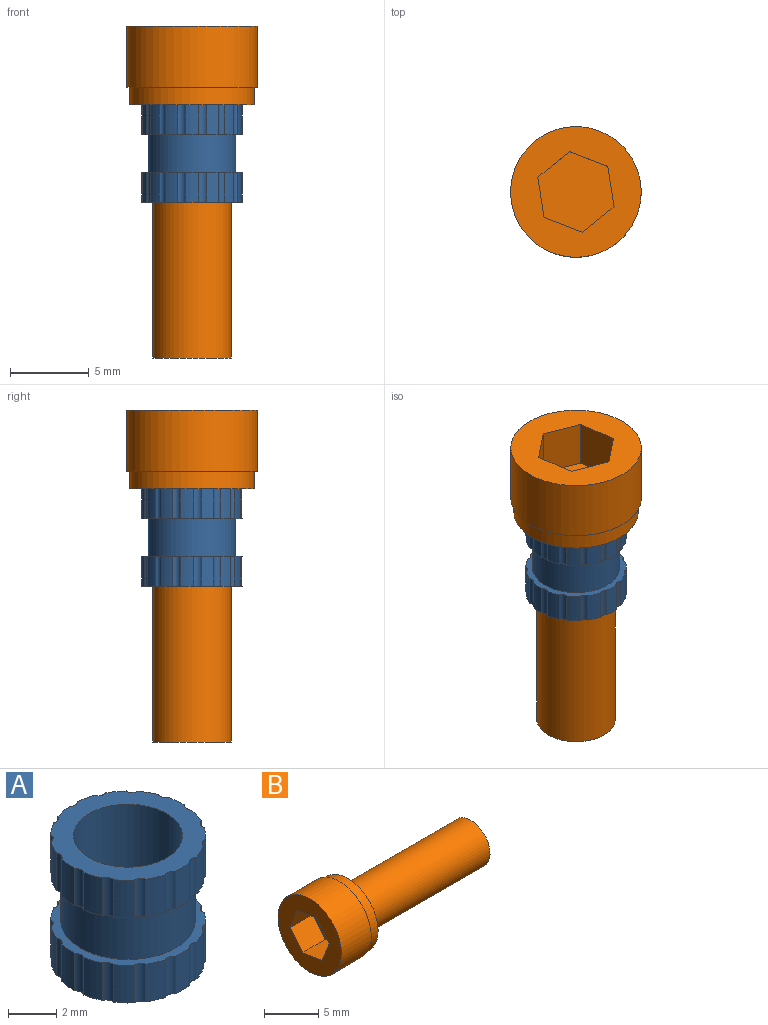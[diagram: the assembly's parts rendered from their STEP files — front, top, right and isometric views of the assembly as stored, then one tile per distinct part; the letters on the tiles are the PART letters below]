
ASSEMBLY  parts=2 mates=1
PART A: 66 faces, bbox 6.4x6.4x6.2 mm
  f0: cylinder r=3.2mm len=1.9mm, axis (0,0,-1), area 1.6mm2, adj f2,f57,f59,f65
  f1: cylinder r=3.2mm len=1.9mm, axis (0,0,-1), area 1.6mm2, adj f3,f61,f63,f64
  f2: cylinder r=0.38mm len=1.9mm, axis (0,0,1), area 1mm2, adj f0,f4,f57,f59
  f3: cylinder r=0.38mm len=1.9mm, axis (0,0,1), area 1mm2, adj f1,f5,f61,f63
  f4: cylinder r=3.2mm len=1.9mm, axis (0,0,-1), area 1.6mm2, adj f2,f6,f57,f59
  f5: cylinder r=3.2mm len=1.9mm, axis (0,0,-1), area 1.6mm2, adj f3,f7,f61,f63
  f6: cylinder r=0.38mm len=1.9mm, axis (0,0,1), area 1mm2, adj f4,f8,f57,f59
  f7: cylinder r=0.38mm len=1.9mm, axis (0,0,1), area 1mm2, adj f5,f9,f61,f63
  f8: cylinder r=3.2mm len=1.9mm, axis (0,0,-1), area 1.6mm2, adj f6,f10,f57,f59
  f9: cylinder r=3.2mm len=1.9mm, axis (0,0,-1), area 1.6mm2, adj f7,f11,f61,f63
  f10: cylinder r=0.38mm len=1.9mm, axis (0,0,1), area 1mm2, adj f8,f12,f57,f59
  f11: cylinder r=0.38mm len=1.9mm, axis (0,0,1), area 1mm2, adj f9,f13,f61,f63
  f12: cylinder r=3.2mm len=1.9mm, axis (0,0,-1), area 1.6mm2, adj f10,f14,f57,f59
  f13: cylinder r=3.2mm len=1.9mm, axis (0,0,-1), area 1.6mm2, adj f11,f15,f61,f63
  f14: cylinder r=0.38mm len=1.9mm, axis (0,0,1), area 1mm2, adj f12,f16,f57,f59
  f15: cylinder r=0.38mm len=1.9mm, axis (0,0,1), area 1mm2, adj f13,f17,f61,f63
  f16: cylinder r=3.2mm len=1.9mm, axis (0,0,-1), area 1.6mm2, adj f14,f18,f57,f59
  f17: cylinder r=3.2mm len=1.9mm, axis (0,0,-1), area 1.6mm2, adj f15,f19,f61,f63
  f18: cylinder r=0.38mm len=1.9mm, axis (0,0,1), area 1mm2, adj f16,f20,f57,f59
  f19: cylinder r=0.38mm len=1.9mm, axis (0,0,1), area 1mm2, adj f17,f21,f61,f63
  f20: cylinder r=3.2mm len=1.9mm, axis (0,0,-1), area 1.6mm2, adj f18,f22,f57,f59
  f21: cylinder r=3.2mm len=1.9mm, axis (0,0,-1), area 1.6mm2, adj f19,f23,f61,f63
  f22: cylinder r=0.38mm len=1.9mm, axis (0,0,1), area 1mm2, adj f20,f24,f57,f59
  f23: cylinder r=0.38mm len=1.9mm, axis (0,0,1), area 1mm2, adj f21,f25,f61,f63
  f24: cylinder r=3.2mm len=1.9mm, axis (0,0,-1), area 1.6mm2, adj f22,f26,f57,f59
  f25: cylinder r=3.2mm len=1.9mm, axis (0,0,-1), area 1.6mm2, adj f23,f27,f61,f63
  f26: cylinder r=0.38mm len=1.9mm, axis (0,0,1), area 1mm2, adj f24,f28,f57,f59
  f27: cylinder r=0.38mm len=1.9mm, axis (0,0,1), area 1mm2, adj f25,f29,f61,f63
  f28: cylinder r=3.2mm len=1.9mm, axis (0,0,-1), area 1.6mm2, adj f26,f30,f57,f59
  f29: cylinder r=3.2mm len=1.9mm, axis (0,0,-1), area 1.6mm2, adj f27,f31,f61,f63
  f30: cylinder r=0.38mm len=1.9mm, axis (0,0,1), area 1mm2, adj f28,f32,f57,f59
  f31: cylinder r=0.38mm len=1.9mm, axis (0,0,1), area 1mm2, adj f29,f33,f61,f63
  f32: cylinder r=3.2mm len=1.9mm, axis (0,0,-1), area 1.6mm2, adj f30,f34,f57,f59
  f33: cylinder r=3.2mm len=1.9mm, axis (0,0,-1), area 1.6mm2, adj f31,f35,f61,f63
  f34: cylinder r=0.38mm len=1.9mm, axis (0,0,1), area 1mm2, adj f32,f36,f57,f59
  f35: cylinder r=0.38mm len=1.9mm, axis (0,0,1), area 1mm2, adj f33,f37,f61,f63
  f36: cylinder r=3.2mm len=1.9mm, axis (0,0,-1), area 1.6mm2, adj f34,f38,f57,f59
  f37: cylinder r=3.2mm len=1.9mm, axis (0,0,-1), area 1.6mm2, adj f35,f39,f61,f63
  f38: cylinder r=0.38mm len=1.9mm, axis (0,0,1), area 1mm2, adj f36,f40,f57,f59
  f39: cylinder r=0.38mm len=1.9mm, axis (0,0,1), area 1mm2, adj f37,f41,f61,f63
  f40: cylinder r=3.2mm len=1.9mm, axis (0,0,-1), area 1.6mm2, adj f38,f42,f57,f59
  f41: cylinder r=3.2mm len=1.9mm, axis (0,0,-1), area 1.6mm2, adj f39,f43,f61,f63
  f42: cylinder r=0.38mm len=1.9mm, axis (0,0,1), area 1mm2, adj f40,f44,f57,f59
  f43: cylinder r=0.38mm len=1.9mm, axis (0,0,1), area 1mm2, adj f41,f45,f61,f63
  f44: cylinder r=3.2mm len=1.9mm, axis (0,0,-1), area 1.6mm2, adj f42,f46,f57,f59
  f45: cylinder r=3.2mm len=1.9mm, axis (0,0,-1), area 1.6mm2, adj f43,f47,f61,f63
  f46: cylinder r=0.38mm len=1.9mm, axis (0,0,1), area 1mm2, adj f44,f48,f57,f59
  f47: cylinder r=0.38mm len=1.9mm, axis (0,0,1), area 1mm2, adj f45,f49,f61,f63
  f48: cylinder r=3.2mm len=1.9mm, axis (0,0,-1), area 1.6mm2, adj f46,f50,f57,f59
  f49: cylinder r=3.2mm len=1.9mm, axis (0,0,-1), area 1.6mm2, adj f47,f51,f61,f63
  f50: cylinder r=0.38mm len=1.9mm, axis (0,0,1), area 1mm2, adj f48,f52,f57,f59
  f51: cylinder r=0.38mm len=1.9mm, axis (0,0,1), area 1mm2, adj f49,f53,f61,f63
  f52: cylinder r=3.2mm len=1.9mm, axis (0,0,-1), area 1.6mm2, adj f50,f54,f57,f59
  f53: cylinder r=3.2mm len=1.9mm, axis (0,0,-1), area 1.6mm2, adj f51,f55,f61,f63
  f54: cylinder r=0.38mm len=1.9mm, axis (0,0,1), area 1mm2, adj f52,f57,f58,f59
  f55: cylinder r=0.38mm len=1.9mm, axis (0,0,1), area 1mm2, adj f53,f61,f62,f63
  f56: cylinder r=2.25mm len=6.2mm, axis (0,0,-1), area 87.7mm2, adj f57,f63
  f57: plane 6.4x6.39mm, normal (0,0,-1), area 15.8mm2, adj f0,f2,f4,f6,f8,f10,f12,f14
  f58: cylinder r=3.2mm len=1.9mm, axis (0,0,-1), area 1.6mm2, adj f54,f57,f59,f65
  f59: plane 6.4x6.39mm, normal (0,0,1), area 7.5mm2, adj f0,f2,f4,f6,f8,f10,f12,f14
  f60: cylinder r=2.77mm len=5.55mm, axis (0,0,-1), area 41.8mm2, adj f59,f61
  f61: plane 6.4x6.39mm, normal (0,0,-1), area 7.5mm2, adj f1,f3,f5,f7,f9,f11,f13,f15
  f62: cylinder r=3.2mm len=1.9mm, axis (0,0,-1), area 1.6mm2, adj f55,f61,f63,f64
  f63: plane 6.4x6.39mm, normal (0,0,1), area 15.8mm2, adj f1,f3,f5,f7,f9,f11,f13,f15
  f64: cylinder r=0.38mm len=1.9mm, axis (0,0,1), area 1mm2, adj f1,f61,f62,f63
  f65: cylinder r=0.38mm len=1.9mm, axis (0,0,1), area 1mm2, adj f0,f57,f58,f59
PART B: 14 faces, bbox 21.1x8.3x8.3 mm
  f0: cylinder r=2.5mm len=16.1mm, axis (-1,0,0), area 252.9mm2, adj f1,f3
  f1: plane 5x5mm, normal (1,0,0), area 19.6mm2, adj f0
  f2: plane 8.3x8.3mm, normal (-1,0,0), area 36.6mm2, adj f6,f7,f8,f9,f10,f11,f12
  f3: plane 7.9x7.9mm, normal (1,0,0), area 29.4mm2, adj f0,f4
  f4: cylinder r=3.95mm len=7.9mm, axis (1,0,0), area 27.3mm2, adj f3,f5
  f5: plane 8.3x8.3mm, normal (1,0,0), area 5.1mm2, adj f4,f6
  f6: cylinder r=4.15mm len=8.3mm, axis (1,0,0), area 101.7mm2, adj f2,f5
  f7: plane 3x2.57mm, normal (0,0.15,0.99), area 7.8mm2, adj f2,f8,f12,f13
  f8: plane 3x2.42mm, normal (0,0.93,0.36), area 7.8mm2, adj f2,f7,f9,f13
  f9: plane 3x2.03mm, normal (0,0.78,-0.63), area 7.8mm2, adj f2,f8,f10,f13
  f10: plane 3x2.57mm, normal (0,-0.15,-0.99), area 7.8mm2, adj f2,f9,f11,f13
  f11: plane 3x2.42mm, normal (0,-0.93,-0.36), area 7.8mm2, adj f2,f10,f12,f13
  f12: plane 3x2.03mm, normal (0,-0.78,0.63), area 7.8mm2, adj f2,f7,f11,f13
  f13: plane 5.14x4.84mm, normal (-1,0,0), area 17.5mm2, adj f7,f8,f9,f10,f11,f12
PLACE A at identity fixed
PLACE B rot(axis=(0.71,0,-0.71),180deg) t=(0,0,6.2)mm
MATE fastened B.f0 <-> A.f0  axis (0,0,-1) through (0,0,6.2)mm
